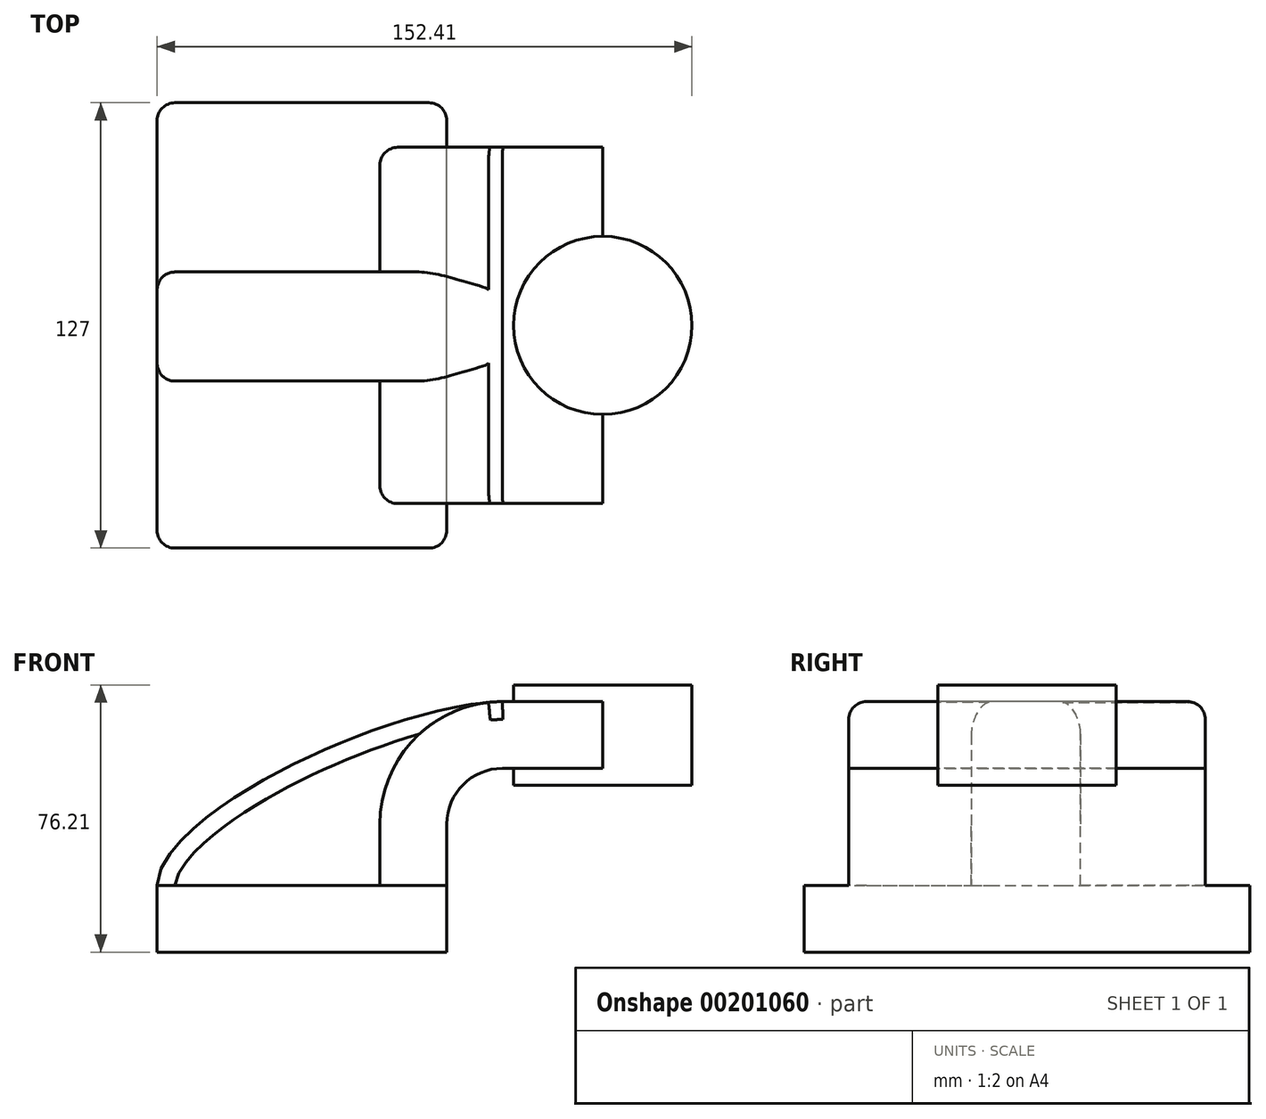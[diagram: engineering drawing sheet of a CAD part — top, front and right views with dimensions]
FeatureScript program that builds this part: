
annotation { "Feature Type Name" : "Feature", "Feature Type Description" : "" }
export const myFeature = defineFeature(function(context is Context, id is Id, definition is map)
    precondition{}
    {
        {
            var Q0;
            Q0=qCreatedBy(makeId("Front.planeOp"),FACE);
            var sketch = newSketch(context, id + "F0", { "sketchPlane" : qUnion([Q0])});
            skLineSegment(sketch, "E0.bottom", {"start": v(-41.28, -9.53) * mm, "end": v(41.28, -9.53) * mm});
            skLineSegment(sketch, "E0.top", {"start": v(-41.28, 9.53) * mm, "end": v(41.28, 9.53) * mm});
            skLineSegment(sketch, "E0.left", {"start": v(-41.28, -9.53) * mm, "end": v(-41.28, 9.53) * mm});
            skLineSegment(sketch, "E0.right", {"start": v(41.28, -9.53) * mm, "end": v(41.28, 9.53) * mm});
            skPoint(sketch, "E0.middle", {"position": v(0, 0) * mm});
            skLineSegment(sketch, "E1.bottom", {"start": v(60.32, 38.1) * mm, "end": v(111.12, 38.1) * mm});
            skLineSegment(sketch, "E1.top", {"start": v(60.32, 66.67) * mm, "end": v(111.12, 66.67) * mm});
            skLineSegment(sketch, "E1.left", {"start": v(60.32, 38.1) * mm, "end": v(60.32, 66.67) * mm});
            skLineSegment(sketch, "E1.right", {"start": v(111.12, 38.1) * mm, "end": v(111.12, 66.67) * mm});
            skPoint(sketch, "E1.middle", {"position": v(85.72, 52.39) * mm});
            skLineSegment(sketch, "E2", {"start": v(41.28, 9.53) * mm, "end": v(41.28, 27) * mm});
            skArc(sketch, "E3", {"start": v(41.27, 27) * mm, "mid": v(45.92, 38.23) * mm, "end": v(57.15, 42.88) * mm});
            skLineSegment(sketch, "E4", {"start": v(57.15, 42.88) * mm, "end": v(85.72, 42.88) * mm});
            skLineSegment(sketch, "E5.0", {"start": v(57.15, 61.93) * mm, "end": v(85.72, 61.93) * mm});
            skArc(sketch, "E5.1", {"start": v(22.22, 27) * mm, "mid": v(32.45, 51.7) * mm, "end": v(57.15, 61.93) * mm});
            skLineSegment(sketch, "E5.2", {"start": v(22.22, 9.53) * mm, "end": v(22.22, 27) * mm});
            skLineSegment(sketch, "E6", {"start": v(85.72, 61.93) * mm, "end": v(85.72, 42.88) * mm});
            skFitSpline(sketch, "E7", {"points": [v(-41.28, 9.53) * mm, v(57.15, 61.93) * mm], "startDerivative": vector(2.04, 62.29) * mm, "endDerivative": vector(98.2, 2.37) * mm});
            skLineSegment(sketch, "E8", {"start": v(85.72, 66.67) * mm, "end": v(85.72, 60.67) * mm});
            skPoint(sketch, "E9", {"position": v(85.72, 38.1) * mm});
            skLineSegment(sketch, "E10", {"start": v(85.72, 42.88) * mm, "end": v(85.72, 38.1) * mm});
            skSolve(sketch);
        }
        {
            var Q0;
            Q0=makeQuery(id+"F0.imprint","IMPRINT",FACE,{"disambiguationData":[TD([[makeQuery(id+"F0.imprint","IMPRINT",EDGE,{"derivedFrom":sQuery(id+"F0.wireOp",EDGE,"E0.bottom")}),1.0]])]});
            extrude(context, id + "F1", {"entities" : qUnion([Q0]), "endBound" : BoundingType.SYMMETRIC, "depth" : 127 * mm});
        }
        {
            var Q0;
            {var subQ5=sQuery(id+"F0.wireOp",EDGE,"E6");Q0=makeQuery(id+"F0.imprint","IMPRINT",FACE,{"disambiguationData":[TD([[makeQuery(id+"F0.imprint","IMPRINT",EDGE,{"derivedFrom":subQ5}),-1.0]])]});}
            var Q1;
            {var subQ1=sQuery(id+"F0.wireOp",EDGE,"E2");Q1=makeQuery(id+"F0.imprint","IMPRINT",FACE,{"disambiguationData":[TD([[makeQuery(id+"F0.imprint","IMPRINT",EDGE,{"derivedFrom":subQ1}),1.0]])]});}
            extrude(context, id + "F2", {"entities" : qUnion([Q0, Q1]), "operationType" : NewBodyOperationType.ADD, "depth" : 50.8 * mm});
        }
        {
            var Q0;
            {var subQ3=sQuery(id+"F0.wireOp",EDGE,"E5.2");Q0=makeQuery(id+"F0.imprint","IMPRINT",FACE,{"disambiguationData":[TD([[makeQuery(id+"F0.imprint","IMPRINT",EDGE,{"derivedFrom":subQ3}),1.0]])]});}
            extrude(context, id + "F3", {"entities" : qUnion([Q0]), "operationType" : NewBodyOperationType.ADD, "depth" : 15.88 * mm});
        }
        {
            var Q0;
            {var subQ1=sQuery(id+"F0.wireOp",EDGE,"E2");Q0=makeQuery(id+"F0.imprint","IMPRINT",FACE,{"disambiguationData":[TD([[makeQuery(id+"F0.imprint","IMPRINT",EDGE,{"derivedFrom":subQ1}),1.0]])]});}
            var Q1;
            {var subQ0=sQuery(id+"F0.wireOp",EDGE,"E6");Q1=makeQuery(id+"F0.imprint","IMPRINT",FACE,{"disambiguationData":[TD([[makeQuery(id+"F0.imprint","IMPRINT",EDGE,{"derivedFrom":subQ0}),-1.0]])]});}
            extrude(context, id + "F4", {"entities" : qUnion([Q0, Q1]), "operationType" : NewBodyOperationType.ADD, "oppositeDirection" : true, "depth" : 50.8 * mm});
        }
        {
            var Q0;
            {var subQ3=sQuery(id+"F0.wireOp",EDGE,"E5.2");Q0=makeQuery(id+"F0.imprint","IMPRINT",FACE,{"disambiguationData":[TD([[makeQuery(id+"F0.imprint","IMPRINT",EDGE,{"derivedFrom":subQ3}),1.0]])]});}
            extrude(context, id + "F5", {"entities" : qUnion([Q0]), "operationType" : NewBodyOperationType.ADD, "oppositeDirection" : true, "depth" : 15.24 * mm});
        }
        {
            var Q0;
            {var subQ0=sQuery(id+"F0.wireOp",EDGE,"E1.right");Q0=makeQuery(id+"F0.imprint","IMPRINT",FACE,{"disambiguationData":[TD([[makeQuery(id+"F0.imprint","IMPRINT",EDGE,{"derivedFrom":subQ0}),1.0]])]});}
            var Q1;
            Q1=sQuery(id+"F0.wireOp",EDGE,"E6");
            revolve(context, id + "F6", {"operationType" : NewBodyOperationType.ADD, "entities" : qUnion([Q0]), "axis" : qUnion([Q1]), "revolveType" : RevolveType.FULL});
        }
        {
            var Q0;
            Q0=makeQuery(id+"F1.opExtrude","CAP_EDGE",EDGE,{"disambiguationData":[OSD([sQuery(id+"F0.wireOp",EDGE,"E0.left")])],"isStart":false});
            var Q1;
            Q1=makeQuery(id+"F1.opExtrude","CAP_EDGE",EDGE,{"disambiguationData":[OSD([sQuery(id+"F0.wireOp",EDGE,"E0.right")])],"isStart":false});
            var Q2;
            Q2=makeQuery(id+"F1.opExtrude","CAP_EDGE",EDGE,{"disambiguationData":[OSD([sQuery(id+"F0.wireOp",EDGE,"E0.right")])],"isStart":true});
            var Q3;
            Q3=makeQuery(id+"F1.opExtrude","CAP_EDGE",EDGE,{"disambiguationData":[OSD([sQuery(id+"F0.wireOp",EDGE,"E0.left")])],"isStart":true});
            var Q4;
            Q4=makeQuery(id+"F4.opExtrude","CAP_EDGE",EDGE,{"disambiguationData":[OSD([sQuery(id+"F0.wireOp",EDGE,"E5.0")])],"isStart":false});
            var Q5;
            Q5=makeQuery(id+"F4.opExtrude","CAP_EDGE",EDGE,{"disambiguationData":[OSD([sQuery(id+"F0.wireOp",EDGE,"E7")])],"isStart":false});
            var Q6;
            Q6=makeQuery(id+"F4.opExtrude","CAP_EDGE",EDGE,{"disambiguationData":[OSD([sQuery(id+"F0.wireOp",EDGE,"E5.1")])],"isStart":false});
            var Q7;
            Q7=makeQuery(id+"F4.opExtrude","CAP_EDGE",EDGE,{"disambiguationData":[OSD([sQuery(id+"F0.wireOp",EDGE,"E5.2")])],"isStart":false});
            var Q8;
            Q8=makeQuery(id+"F5.opExtrude","CAP_EDGE",EDGE,{"disambiguationData":[OSD([sQuery(id+"F0.wireOp",EDGE,"E7")])],"isStart":false});
            var Q9;
            Q9=makeQuery(id+"F3.opExtrude","CAP_EDGE",EDGE,{"disambiguationData":[OSD([sQuery(id+"F0.wireOp",EDGE,"E7")])],"isStart":false});
            var Q10;
            Q10=makeQuery(id+"F2.opExtrude","CAP_EDGE",EDGE,{"disambiguationData":[OSD([sQuery(id+"F0.wireOp",EDGE,"E5.1")])],"isStart":false});
            var Q11;
            Q11=makeQuery(id+"F2.opExtrude","CAP_EDGE",EDGE,{"disambiguationData":[OSD([sQuery(id+"F0.wireOp",EDGE,"E7")])],"isStart":false});
            var Q12;
            Q12=makeQuery(id+"F2.opExtrude","CAP_EDGE",EDGE,{"disambiguationData":[OSD([sQuery(id+"F0.wireOp",EDGE,"E5.0")])],"isStart":false});
            fillet(context, id + "F7", {"entities" : qUnion([Q0, Q1, Q2, Q3, Q4, Q5, Q6, Q7, Q8, Q9, Q10, Q11, Q12]), "radius" : 5.08 * mm, "tangentPropagation" : true, "allowEdgeOverflow" : false});
        }
    });
